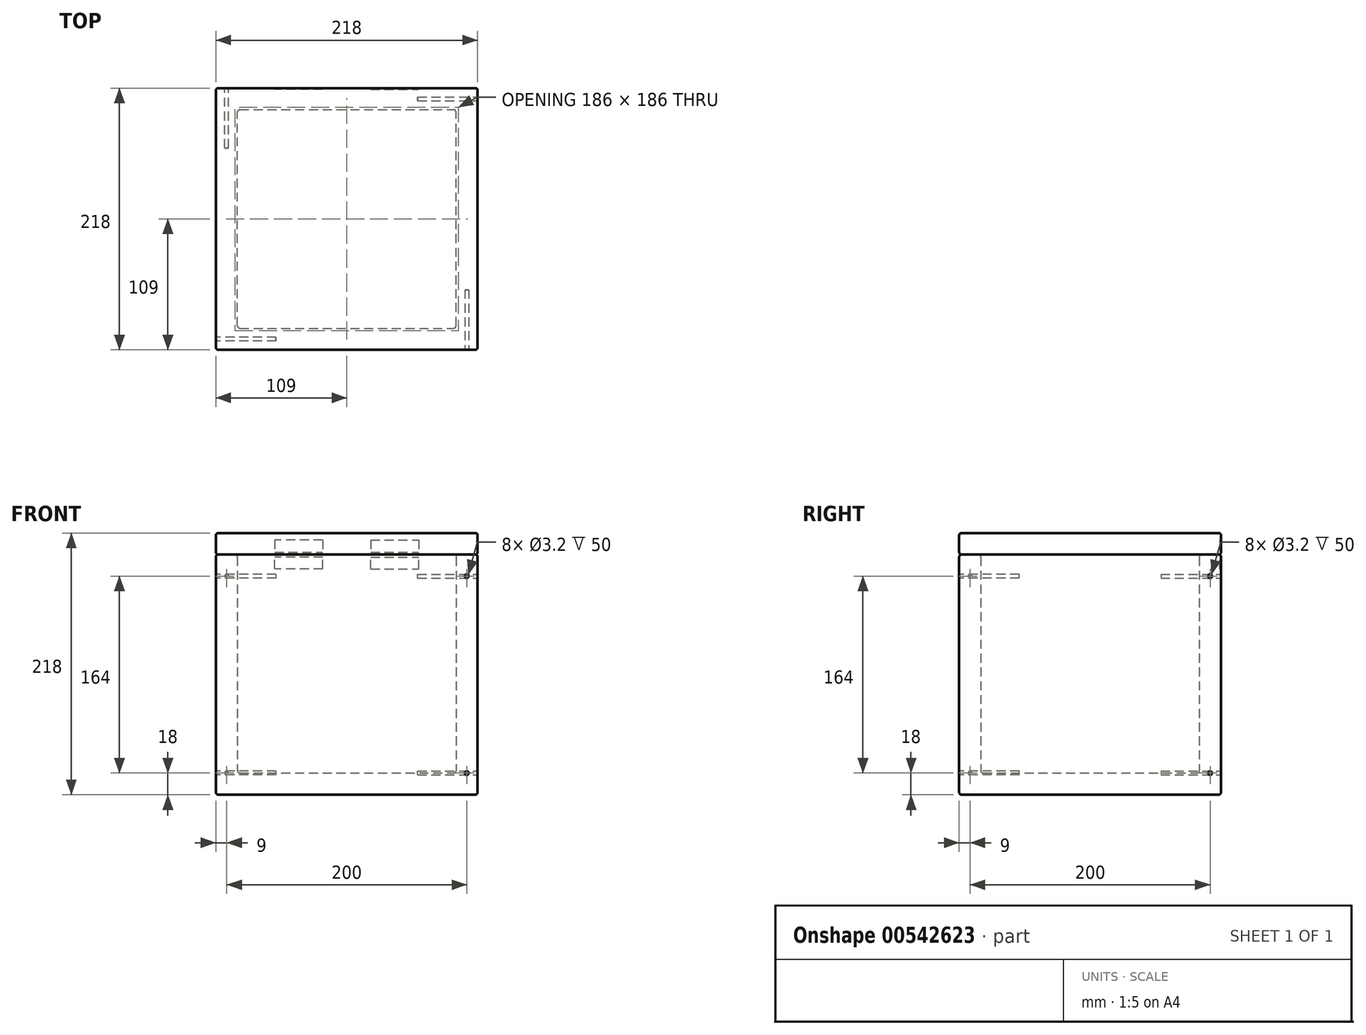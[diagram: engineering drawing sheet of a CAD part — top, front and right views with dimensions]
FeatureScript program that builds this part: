
annotation { "Feature Type Name" : "Feature", "Feature Type Description" : "" }
export const myFeature = defineFeature(function(context is Context, id is Id, definition is map)
    precondition{}
    {
        {
            var Q0;
            Q0=qCreatedBy(makeId("Top.planeOp"),FACE);
            var sketch = newSketch(context, id + "F0", { "sketchPlane" : qUnion([Q0])});
            skLineSegment(sketch, "E0.bottom", {"start": v(-109, -109) * mm, "end": v(109, -109) * mm});
            skLineSegment(sketch, "E0.top", {"start": v(-109, 109) * mm, "end": v(109, 109) * mm});
            skLineSegment(sketch, "E0.left", {"start": v(-109, -109) * mm, "end": v(-109, 109) * mm});
            skLineSegment(sketch, "E0.right", {"start": v(109, -109) * mm, "end": v(109, 109) * mm});
            skPoint(sketch, "E0.middle", {"position": v(0, 0) * mm});
            skSolve(sketch);
        }
        {
            var Q0;
            Q0 = qSketchRegion(id + "F0", true);
            extrude(context, id + "F1", {"entities" : qUnion([Q0]), "depth" : 200 * mm, "offsetDistance" : 25.4 * mm});
        }
        {
            var Q0;
            Q0=makeQuery(id+"F1.opExtrude","CAP_FACE",FACE,{"disambiguationData":[OSD([sQuery(id+"F0.wireOp",EDGE,"E0.bottom"),sQuery(id+"F0.wireOp",EDGE,"E0.top"),sQuery(id+"F0.wireOp",EDGE,"E0.left"),sQuery(id+"F0.wireOp",EDGE,"E0.right")])],"isStart":false});
            shell(context, id + "F2", {"entities" : qUnion([Q0]), "thickness" : 18 * mm});
        }
        {
            var Q0;
            Q0=makeQuery(id+"F1.opExtrude","CAP_FACE",FACE,{"disambiguationData":[OSD([sQuery(id+"F0.wireOp",EDGE,"E0.bottom"),sQuery(id+"F0.wireOp",EDGE,"E0.top"),sQuery(id+"F0.wireOp",EDGE,"E0.left"),sQuery(id+"F0.wireOp",EDGE,"E0.right")])],"isStart":false});
            var sketch = newSketch(context, id + "F3", { "sketchPlane" : qUnion([Q0])});
            skLineSegment(sketch, "E1.bottom", {"start": v(-109, -109) * mm, "end": v(109, -109) * mm});
            skLineSegment(sketch, "E1.top", {"start": v(-109, 109) * mm, "end": v(109, 109) * mm});
            skLineSegment(sketch, "E1.left", {"start": v(-109, -109) * mm, "end": v(-109, 109) * mm});
            skLineSegment(sketch, "E1.right", {"start": v(109, -109) * mm, "end": v(109, 109) * mm});
            skPoint(sketch, "E1.middle", {"position": v(0, 0) * mm});
            skSolve(sketch);
        }
        {
            var Q0;
            Q0=makeQuery(id+"F3.imprint","IMPRINT",FACE,{"disambiguationData":[TD([[makeQuery(id+"F3.imprint","IMPRINT",EDGE,{"derivedFrom":sQuery(id+"F3.wireOp",EDGE,"E1.bottom")}),1.0]])]});
            var Q1;
            {var subQ0=sQuery(id+"F0.wireOp",EDGE,"E0.bottom");Q1=makeQuery(id+"F3.imprint","IMPRINT",FACE,{"disambiguationData":[TD([[makeQuery(id+"F3.imprint","IMPRINT",EDGE,{"derivedFrom":makeQuery(id+"F2.opShell","OFFSET_EDGE",EDGE,{"disambiguationData":[OSD([subQ0]),TDD([makeQuery(id+"F1.opExtrude","CAP_EDGE",EDGE,{"disambiguationData":[OSD([subQ0])],"isStart":false})])]})}),1.0]])]});}
            extrude(context, id + "F4", {"entities" : qUnion([Q0, Q1]), "depth" : 18 * mm, "offsetDistance" : 25.4 * mm});
        }
        {
            var Q0;
            Q0=makeQuery(id+"F4.opExtrude","CAP_EDGE",EDGE,{"disambiguationData":[OSD([sQuery(id+"F3.wireOp",EDGE,"E1.top")])],"isStart":true});
            var Q1;
            Q1=makeQuery(id+"F4.opExtrude","CAP_EDGE",EDGE,{"disambiguationData":[OSD([sQuery(id+"F3.wireOp",EDGE,"E1.left")])],"isStart":true});
            var Q2;
            Q2=makeQuery(id+"F4.opExtrude","CAP_EDGE",EDGE,{"disambiguationData":[OSD([sQuery(id+"F3.wireOp",EDGE,"E1.bottom")])],"isStart":true});
            var Q3;
            Q3=makeQuery(id+"F4.opExtrude","CAP_EDGE",EDGE,{"disambiguationData":[OSD([sQuery(id+"F3.wireOp",EDGE,"E1.right")])],"isStart":true});
            var Q4;
            Q4=makeQuery(id+"F4.opExtrude","CAP_EDGE",EDGE,{"disambiguationData":[OSD([sQuery(id+"F3.wireOp",EDGE,"E1.top")])],"isStart":false});
            var Q5;
            Q5=makeQuery(id+"F4.opExtrude","CAP_EDGE",EDGE,{"disambiguationData":[OSD([sQuery(id+"F3.wireOp",EDGE,"E1.left")])],"isStart":false});
            var Q6;
            Q6=makeQuery(id+"F4.opExtrude","CAP_EDGE",EDGE,{"disambiguationData":[OSD([sQuery(id+"F3.wireOp",EDGE,"E1.bottom")])],"isStart":false});
            var Q7;
            Q7=makeQuery(id+"F4.opExtrude","CAP_EDGE",EDGE,{"disambiguationData":[OSD([sQuery(id+"F3.wireOp",EDGE,"E1.right")])],"isStart":false});
            var Q8;
            Q8=makeQuery(id+"F4.opExtrude","SWEPT_EDGE",EDGE,{"disambiguationData":[OSD([sQuery(id+"F3.wireOp",EDGE,"E1.top"),sQuery(id+"F3.wireOp",EDGE,"E1.right")])]});
            var Q9;
            Q9=makeQuery(id+"F4.opExtrude","SWEPT_EDGE",EDGE,{"disambiguationData":[OSD([sQuery(id+"F3.wireOp",EDGE,"E1.bottom"),sQuery(id+"F3.wireOp",EDGE,"E1.right")])]});
            var Q10;
            Q10=makeQuery(id+"F4.opExtrude","SWEPT_EDGE",EDGE,{"disambiguationData":[OSD([sQuery(id+"F3.wireOp",EDGE,"E1.top"),sQuery(id+"F3.wireOp",EDGE,"E1.left")])]});
            var Q11;
            Q11=makeQuery(id+"F4.opExtrude","SWEPT_EDGE",EDGE,{"disambiguationData":[OSD([sQuery(id+"F3.wireOp",EDGE,"E1.bottom"),sQuery(id+"F3.wireOp",EDGE,"E1.left")])]});
            fillet(context, id + "F5", {"entities" : qUnion([Q0, Q1, Q2, Q3, Q4, Q5, Q6, Q7, Q8, Q9, Q10, Q11]), "radius" : 2 * mm, "tangentPropagation" : true, "allowEdgeOverflow" : false});
        }
        {
            var Q0;
            Q0=makeQuery(id+"F1.opExtrude","CAP_EDGE",EDGE,{"disambiguationData":[OSD([sQuery(id+"F0.wireOp",EDGE,"E0.left")])],"isStart":false});
            var Q1;
            {var subQ0=sQuery(id+"F0.wireOp",EDGE,"E0.left");Q1=makeQuery(id+"F2.opShell","OFFSET_EDGE",EDGE,{"disambiguationData":[OSD([subQ0]),TDD([makeQuery(id+"F1.opExtrude","CAP_EDGE",EDGE,{"disambiguationData":[OSD([subQ0])],"isStart":false})])]});}
            var Q2;
            {var subQ0=sQuery(id+"F0.wireOp",EDGE,"E0.top");Q2=makeQuery(id+"F2.opShell","OFFSET_EDGE",EDGE,{"disambiguationData":[OSD([subQ0]),TDD([makeQuery(id+"F1.opExtrude","CAP_EDGE",EDGE,{"disambiguationData":[OSD([subQ0])],"isStart":false})])]});}
            var Q3;
            {var subQ0=sQuery(id+"F0.wireOp",EDGE,"E0.right");Q3=makeQuery(id+"F2.opShell","OFFSET_EDGE",EDGE,{"disambiguationData":[OSD([subQ0]),TDD([makeQuery(id+"F1.opExtrude","CAP_EDGE",EDGE,{"disambiguationData":[OSD([subQ0])],"isStart":false})])]});}
            var Q4;
            {var subQ0=sQuery(id+"F0.wireOp",EDGE,"E0.bottom");Q4=makeQuery(id+"F2.opShell","OFFSET_EDGE",EDGE,{"disambiguationData":[OSD([subQ0]),TDD([makeQuery(id+"F1.opExtrude","CAP_EDGE",EDGE,{"disambiguationData":[OSD([subQ0])],"isStart":false})])]});}
            var Q5;
            Q5=makeQuery(id+"F2.opShell","OFFSET_EDGE",EDGE,{"disambiguationData":[OSD([sQuery(id+"F0.wireOp",EDGE,"E0.bottom"),sQuery(id+"F0.wireOp",EDGE,"E0.left")])]});
            var Q6;
            {var subQ0=sQuery(id+"F0.wireOp",EDGE,"E0.left");Q6=makeQuery(id+"F2.opShell","OFFSET_EDGE",EDGE,{"disambiguationData":[OSD([subQ0]),TDD([makeQuery(id+"F1.opExtrude","CAP_EDGE",EDGE,{"disambiguationData":[OSD([subQ0])],"isStart":true})])]});}
            var Q7;
            Q7=makeQuery(id+"F2.opShell","OFFSET_EDGE",EDGE,{"disambiguationData":[OSD([sQuery(id+"F0.wireOp",EDGE,"E0.top"),sQuery(id+"F0.wireOp",EDGE,"E0.left")])]});
            var Q8;
            {var subQ0=sQuery(id+"F0.wireOp",EDGE,"E0.top");Q8=makeQuery(id+"F2.opShell","OFFSET_EDGE",EDGE,{"disambiguationData":[OSD([subQ0]),TDD([makeQuery(id+"F1.opExtrude","CAP_EDGE",EDGE,{"disambiguationData":[OSD([subQ0])],"isStart":true})])]});}
            var Q9;
            Q9=makeQuery(id+"F2.opShell","OFFSET_EDGE",EDGE,{"disambiguationData":[OSD([sQuery(id+"F0.wireOp",EDGE,"E0.top"),sQuery(id+"F0.wireOp",EDGE,"E0.right")])]});
            var Q10;
            Q10=makeQuery(id+"F2.opShell","OFFSET_EDGE",EDGE,{"disambiguationData":[OSD([sQuery(id+"F0.wireOp",EDGE,"E0.bottom"),sQuery(id+"F0.wireOp",EDGE,"E0.right")])]});
            var Q11;
            {var subQ0=sQuery(id+"F0.wireOp",EDGE,"E0.right");Q11=makeQuery(id+"F2.opShell","OFFSET_EDGE",EDGE,{"disambiguationData":[OSD([subQ0]),TDD([makeQuery(id+"F1.opExtrude","CAP_EDGE",EDGE,{"disambiguationData":[OSD([subQ0])],"isStart":true})])]});}
            var Q12;
            {var subQ0=sQuery(id+"F0.wireOp",EDGE,"E0.bottom");Q12=makeQuery(id+"F2.opShell","OFFSET_EDGE",EDGE,{"disambiguationData":[OSD([subQ0]),TDD([makeQuery(id+"F1.opExtrude","CAP_EDGE",EDGE,{"disambiguationData":[OSD([subQ0])],"isStart":true})])]});}
            var Q13;
            Q13=makeQuery(id+"F1.opExtrude","CAP_EDGE",EDGE,{"disambiguationData":[OSD([sQuery(id+"F0.wireOp",EDGE,"E0.top")])],"isStart":false});
            var Q14;
            Q14=makeQuery(id+"F1.opExtrude","CAP_EDGE",EDGE,{"disambiguationData":[OSD([sQuery(id+"F0.wireOp",EDGE,"E0.right")])],"isStart":false});
            var Q15;
            Q15=makeQuery(id+"F1.opExtrude","CAP_EDGE",EDGE,{"disambiguationData":[OSD([sQuery(id+"F0.wireOp",EDGE,"E0.bottom")])],"isStart":false});
            var Q16;
            Q16=makeQuery(id+"F1.opExtrude","CAP_EDGE",EDGE,{"disambiguationData":[OSD([sQuery(id+"F0.wireOp",EDGE,"E0.bottom")])],"isStart":true});
            var Q17;
            Q17=makeQuery(id+"F1.opExtrude","SWEPT_EDGE",EDGE,{"disambiguationData":[OSD([sQuery(id+"F0.wireOp",EDGE,"E0.bottom"),sQuery(id+"F0.wireOp",EDGE,"E0.left")])]});
            var Q18;
            Q18=makeQuery(id+"F1.opExtrude","SWEPT_EDGE",EDGE,{"disambiguationData":[OSD([sQuery(id+"F0.wireOp",EDGE,"E0.bottom"),sQuery(id+"F0.wireOp",EDGE,"E0.right")])]});
            var Q19;
            Q19=makeQuery(id+"F1.opExtrude","CAP_EDGE",EDGE,{"disambiguationData":[OSD([sQuery(id+"F0.wireOp",EDGE,"E0.right")])],"isStart":true});
            var Q20;
            Q20=makeQuery(id+"F1.opExtrude","SWEPT_EDGE",EDGE,{"disambiguationData":[OSD([sQuery(id+"F0.wireOp",EDGE,"E0.top"),sQuery(id+"F0.wireOp",EDGE,"E0.right")])]});
            var Q21;
            Q21=makeQuery(id+"F1.opExtrude","CAP_EDGE",EDGE,{"disambiguationData":[OSD([sQuery(id+"F0.wireOp",EDGE,"E0.top")])],"isStart":true});
            var Q22;
            Q22=makeQuery(id+"F1.opExtrude","SWEPT_EDGE",EDGE,{"disambiguationData":[OSD([sQuery(id+"F0.wireOp",EDGE,"E0.top"),sQuery(id+"F0.wireOp",EDGE,"E0.left")])]});
            var Q23;
            Q23=makeQuery(id+"F1.opExtrude","CAP_EDGE",EDGE,{"disambiguationData":[OSD([sQuery(id+"F0.wireOp",EDGE,"E0.left")])],"isStart":true});
            fillet(context, id + "F6", {"entities" : qUnion([Q0, Q1, Q2, Q3, Q4, Q5, Q6, Q7, Q8, Q9, Q10, Q11, Q12, Q13, Q14, Q15, Q16, Q17, Q18, Q19, Q20, Q21, Q22, Q23]), "radius" : 2 * mm, "tangentPropagation" : true, "allowEdgeOverflow" : false});
        }
        {
            var Q0;
            Q0=makeQuery(id+"F4.opExtrude","SWEPT_FACE",FACE,{"disambiguationData":[OSD([sQuery(id+"F3.wireOp",EDGE,"E1.top")])]});
            var sketch = newSketch(context, id + "F7", { "sketchPlane" : qUnion([Q0])});
            skLineSegment(sketch, "E2.bottom", {"start": v(-20, 212) * mm, "end": v(-60, 212) * mm});
            skLineSegment(sketch, "E2.top", {"start": v(-20, 202) * mm, "end": v(-60, 202) * mm});
            skLineSegment(sketch, "E2.left", {"start": v(-20, 212) * mm, "end": v(-20, 202) * mm});
            skLineSegment(sketch, "E2.right", {"start": v(-60, 212) * mm, "end": v(-60, 202) * mm});
            skLineSegment(sketch, "E3.MirrorCS", {"start": v(-20, 198) * mm, "end": v(-60, 198) * mm});
            skLineSegment(sketch, "E4.MirrorCS", {"start": v(-20, 188) * mm, "end": v(-20, 198) * mm});
            skLineSegment(sketch, "E5.MirrorCS", {"start": v(-20, 188) * mm, "end": v(-60, 188) * mm});
            skLineSegment(sketch, "E6.MirrorCS", {"start": v(-60, 188) * mm, "end": v(-60, 198) * mm});
            skLineSegment(sketch, "E7.MirrorCS", {"start": v(20, 202) * mm, "end": v(60, 202) * mm});
            skLineSegment(sketch, "E8.MirrorCS", {"start": v(20, 212) * mm, "end": v(20, 202) * mm});
            skLineSegment(sketch, "E9.MirrorCS", {"start": v(20, 212) * mm, "end": v(60, 212) * mm});
            skLineSegment(sketch, "E10.MirrorCS", {"start": v(60, 212) * mm, "end": v(60, 202) * mm});
            skLineSegment(sketch, "E11.MirrorCS", {"start": v(20, 198) * mm, "end": v(60, 198) * mm});
            skLineSegment(sketch, "E12.MirrorCS", {"start": v(20, 188) * mm, "end": v(60, 188) * mm});
            skLineSegment(sketch, "E13.MirrorCS", {"start": v(20, 188) * mm, "end": v(20, 198) * mm});
            skLineSegment(sketch, "E14.MirrorCS", {"start": v(60, 188) * mm, "end": v(60, 198) * mm});
            skSolve(sketch);
        }
        {
            var Q0;
            Q0 = qSketchRegion(id + "F7", true);
            extrude(context, id + "F8", {"entities" : qUnion([Q0]), "operationType" : NewBodyOperationType.REMOVE, "oppositeDirection" : true, "depth" : 1 * mm, "offsetDistance" : 25.4 * mm});
        }
        {
            var Q0;
            Q0=makeQuery(id+"F1.opExtrude","SWEPT_FACE",FACE,{"disambiguationData":[OSD([sQuery(id+"F0.wireOp",EDGE,"E0.top")])]});
            var sketch = newSketch(context, id + "F9", { "sketchPlane" : qUnion([Q0])});
            skCircle(sketch, "E15.MirrorC", {"center": v(100, 18) * mm, "radius": 1.6 * mm});
            skCircle(sketch, "E16.MirrorC", {"center": v(100, 182) * mm, "radius": 1.6 * mm});
            skSolve(sketch);
        }
        {
            var Q0;
            Q0 = qSketchRegion(id + "F9", true);
            extrude(context, id + "F10", {"entities" : qUnion([Q0]), "operationType" : NewBodyOperationType.REMOVE, "oppositeDirection" : true, "depth" : 50 * mm, "offsetDistance" : 25.4 * mm});
        }
        {
            var Q0;
            Q0=makeQuery(id+"F1.opExtrude","SWEPT_FACE",FACE,{"disambiguationData":[OSD([sQuery(id+"F0.wireOp",EDGE,"E0.right")])]});
            var sketch = newSketch(context, id + "F11", { "sketchPlane" : qUnion([Q0])});
            skPoint(sketch, "E17", {"position": v(100, 182) * mm});
            skCircle(sketch, "E18", {"center": v(100, 182) * mm, "radius": 1.6 * mm});
            skPoint(sketch, "E19.MirrorP", {"position": v(100, 18) * mm});
            skCircle(sketch, "E20.MirrorC", {"center": v(100, 18) * mm, "radius": 1.6 * mm});
            skSolve(sketch);
        }
        {
            var Q0;
            Q0 = qSketchRegion(id + "F11", true);
            extrude(context, id + "F12", {"entities" : qUnion([Q0]), "operationType" : NewBodyOperationType.REMOVE, "oppositeDirection" : true, "depth" : 50 * mm, "offsetDistance" : 25.4 * mm});
        }
        {
            var Q0;
            Q0=makeQuery(id+"F1.opExtrude","SWEPT_FACE",FACE,{"disambiguationData":[OSD([sQuery(id+"F0.wireOp",EDGE,"E0.bottom")])]});
            var sketch = newSketch(context, id + "F13", { "sketchPlane" : qUnion([Q0])});
            skPoint(sketch, "E21", {"position": v(100, 182) * mm});
            skCircle(sketch, "E22", {"center": v(100, 182) * mm, "radius": 1.6 * mm});
            skCircle(sketch, "E23.MirrorC", {"center": v(100, 18) * mm, "radius": 1.6 * mm});
            skSolve(sketch);
        }
        {
            var Q0;
            Q0 = qSketchRegion(id + "F13", true);
            extrude(context, id + "F14", {"entities" : qUnion([Q0]), "operationType" : NewBodyOperationType.REMOVE, "oppositeDirection" : true, "depth" : 50 * mm, "offsetDistance" : 25.4 * mm});
        }
        {
            var Q0;
            Q0=makeQuery(id+"F1.opExtrude","SWEPT_FACE",FACE,{"disambiguationData":[OSD([sQuery(id+"F0.wireOp",EDGE,"E0.left")])]});
            var sketch = newSketch(context, id + "F15", { "sketchPlane" : qUnion([Q0])});
            skPoint(sketch, "E24", {"position": v(100, 182) * mm});
            skCircle(sketch, "E25", {"center": v(100, 182) * mm, "radius": 1.6 * mm});
            skCircle(sketch, "E26.MirrorC", {"center": v(100, 18) * mm, "radius": 1.6 * mm});
            skSolve(sketch);
        }
        {
            var Q0;
            Q0 = qSketchRegion(id + "F15", true);
            extrude(context, id + "F16", {"entities" : qUnion([Q0]), "operationType" : NewBodyOperationType.REMOVE, "oppositeDirection" : true, "depth" : 50 * mm, "offsetDistance" : 25.4 * mm});
        }
    });
